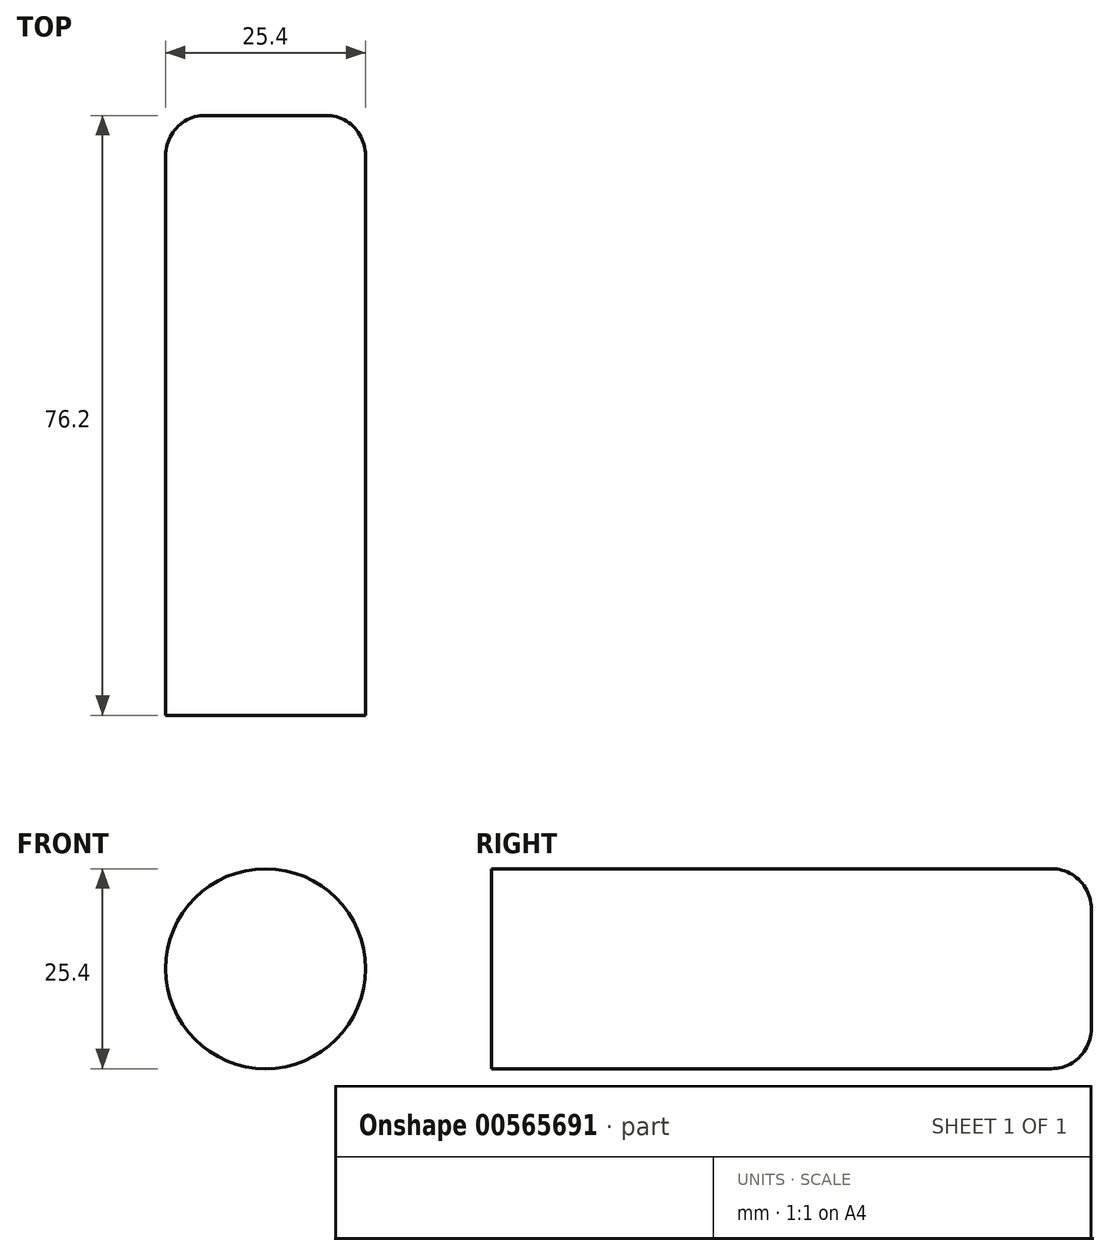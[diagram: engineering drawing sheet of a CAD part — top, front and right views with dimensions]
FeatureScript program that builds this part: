
annotation { "Feature Type Name" : "Feature", "Feature Type Description" : "" }
export const myFeature = defineFeature(function(context is Context, id is Id, definition is map)
    precondition{}
    {
        {
            var Q0;
            Q0=qCreatedBy(makeId("Front.planeOp"),FACE);
            var sketch = newSketch(context, id + "F0", { "sketchPlane" : qUnion([Q0])});
            skCircle(sketch, "E0", {"center": v(0, 0) * mm, "radius": 12.7 * mm});
            skSolve(sketch);
        }
        {
            var Q0;
            Q0=makeQuery(id+"F0.imprint","IMPRINT",FACE,{"disambiguationData":[TD([[makeQuery(id+"F0.imprint","IMPRINT",EDGE,{"derivedFrom":sQuery(id+"F0.wireOp",EDGE,"E0")}),1.0]])]});
            extrude(context, id + "F1", {"entities" : qUnion([Q0]), "depth" : 76.2 * mm, "offsetDistance" : 25.4 * mm});
        }
        {
            var Q0;
            Q0=makeQuery(id+"F1.opExtrude","CAP_EDGE",EDGE,{"disambiguationData":[OSD([sQuery(id+"F0.wireOp",EDGE,"E0")])],"isStart":true});
            fillet(context, id + "F2", {"entities" : qUnion([Q0]), "radius" : 5.08 * mm, "tangentPropagation" : true, "allowEdgeOverflow" : false});
        }
    });
